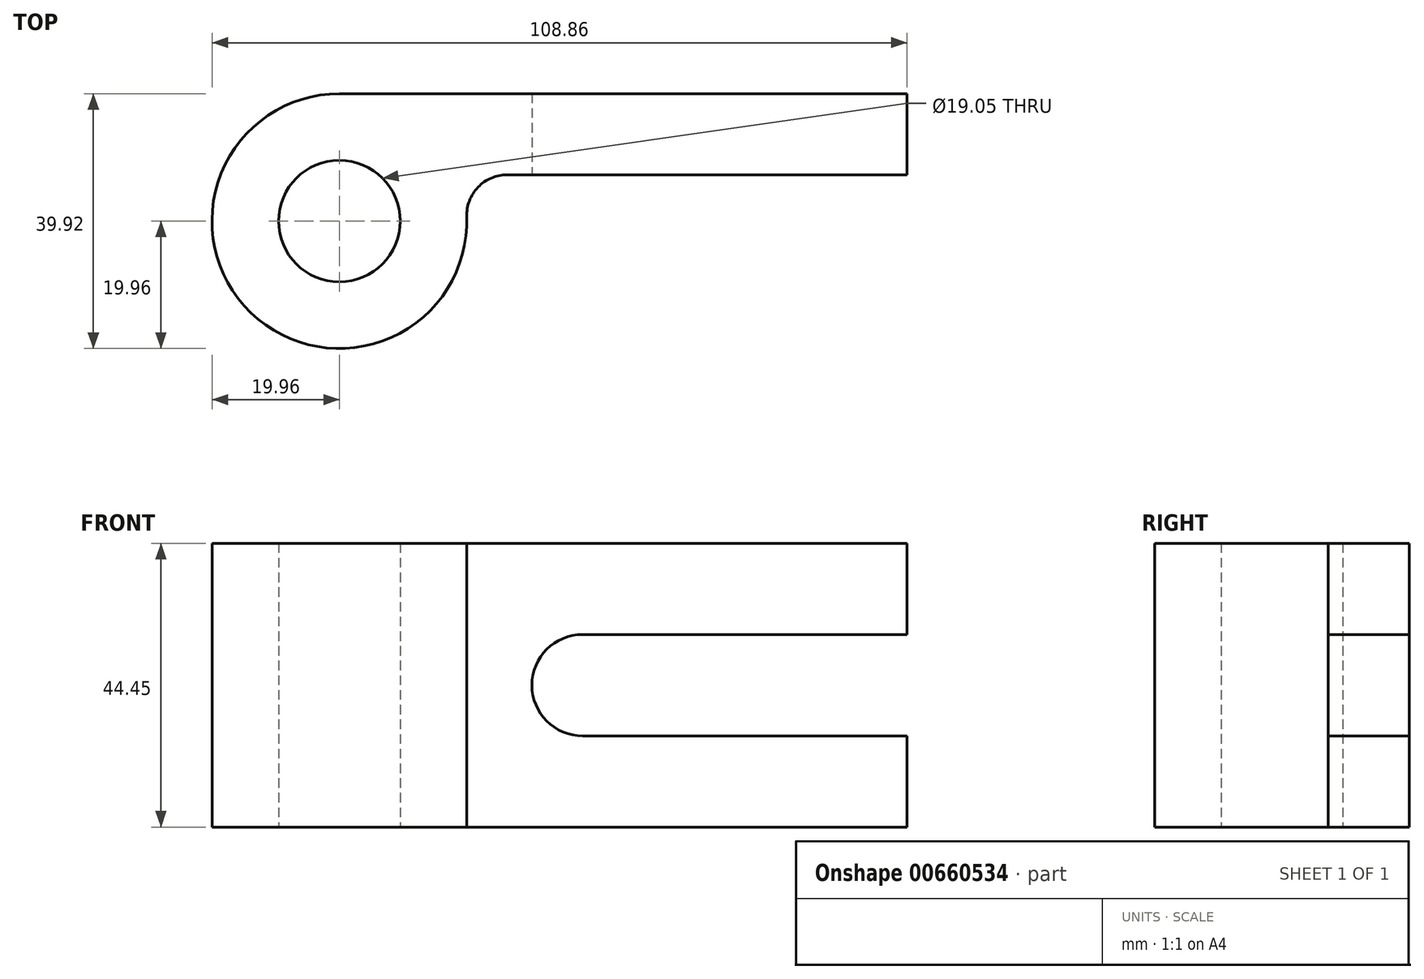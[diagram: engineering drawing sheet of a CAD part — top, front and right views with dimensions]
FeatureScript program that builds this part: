
annotation { "Feature Type Name" : "Feature", "Feature Type Description" : "" }
export const myFeature = defineFeature(function(context is Context, id is Id, definition is map)
    precondition{}
    {
        {
            var Q0;
            Q0=qCreatedBy(makeId("Top.planeOp"),FACE);
            var sketch = newSketch(context, id + "F0", { "sketchPlane" : qUnion([Q0])});
            skCircle(sketch, "E0", {"center": v(0, 0) * mm, "radius": 9.53 * mm});
            skCircle(sketch, "E1", {"center": v(0, 0) * mm, "radius": 19.96 * mm});
            skLineSegment(sketch, "E2", {"start": v(0, 19.96) * mm, "end": v(88.9, 19.96) * mm});
            skLineSegment(sketch, "E3", {"start": v(88.9, 19.96) * mm, "end": v(88.9, 7.26) * mm});
            skLineSegment(sketch, "E4", {"start": v(88.9, 7.26) * mm, "end": v(18.6, 7.26) * mm});
            skSolve(sketch);
        }
        {
            var Q0;
            {var subQ0=sQuery(id+"F0.wireOp",EDGE,"E2");Q0=makeQuery(id+"F0.imprint","IMPRINT",FACE,{"disambiguationData":[TD([[makeQuery(id+"F0.imprint","IMPRINT",EDGE,{"derivedFrom":subQ0}),-1.0]])]});}
            var Q1;
            Q1=makeQuery(id+"F0.imprint","IMPRINT",FACE,{"disambiguationData":[TD([[makeQuery(id+"F0.imprint","IMPRINT",EDGE,{"derivedFrom":sQuery(id+"F0.wireOp",EDGE,"E0")}),-1.0]])]});
            extrude(context, id + "F1", {"entities" : qUnion([Q0, Q1]), "depth" : 44.45 * mm, "offsetDistance" : 25.4 * mm});
        }
        {
            var Q0;
            Q0=makeQuery(id+"F1.opExtrude","SWEPT_FACE",FACE,{"disambiguationData":[OSD([sQuery(id+"F0.wireOp",EDGE,"E4")])]});
            var sketch = newSketch(context, id + "F2", { "sketchPlane" : qUnion([Q0])});
            skLineSegment(sketch, "E5.bottom", {"start": v(88.9, 30.15) * mm, "end": v(38.1, 30.15) * mm});
            skLineSegment(sketch, "E5.top", {"start": v(88.9, 14.27) * mm, "end": v(38.1, 14.27) * mm});
            skLineSegment(sketch, "E5.left", {"start": v(88.9, 30.15) * mm, "end": v(88.9, 14.27) * mm});
            skLineSegment(sketch, "E5.right", {"start": v(38.1, 30.15) * mm, "end": v(38.1, 14.27) * mm});
            skCircle(sketch, "E6", {"center": v(38.1, 22.21) * mm, "radius": 7.94 * mm});
            skSolve(sketch);
        }
        {
            var Q0;
            {var subQ0=sQuery(id+"F2.wireOp",EDGE,"E5.bottom");Q0=makeQuery(id+"F2.imprint","IMPRINT",FACE,{"disambiguationData":[TD([[makeQuery(id+"F2.imprint","IMPRINT",EDGE,{"derivedFrom":subQ0}),1.0]])]});}
            var Q1;
            {var subQ0=sQuery(id+"F2.wireOp",EDGE,"E5.right");Q1=makeQuery(id+"F2.imprint","IMPRINT",FACE,{"disambiguationData":[TD([[makeQuery(id+"F2.imprint","IMPRINT",EDGE,{"derivedFrom":subQ0}),-1.0]])]});}
            var Q2;
            {var subQ0=sQuery(id+"F2.wireOp",EDGE,"E5.right");Q2=makeQuery(id+"F2.imprint","IMPRINT",FACE,{"disambiguationData":[TD([[makeQuery(id+"F2.imprint","IMPRINT",EDGE,{"derivedFrom":subQ0}),1.0]])]});}
            extrude(context, id + "F3", {"entities" : qUnion([Q0, Q1, Q2]), "operationType" : NewBodyOperationType.REMOVE, "oppositeDirection" : true, "depth" : 12.7 * mm, "offsetDistance" : 25.4 * mm});
        }
        {
            var Q0;
            Q0=makeQuery(id+"F1.opExtrude","SWEPT_EDGE",EDGE,{"disambiguationData":[OSD([sQuery(id+"F0.wireOp",EDGE,"E1"),sQuery(id+"F0.wireOp",EDGE,"E4")])]});
            fillet(context, id + "F4", {"entities" : qUnion([Q0]), "radius" : 6.35 * mm, "tangentPropagation" : true, "allowEdgeOverflow" : false});
        }
    });
